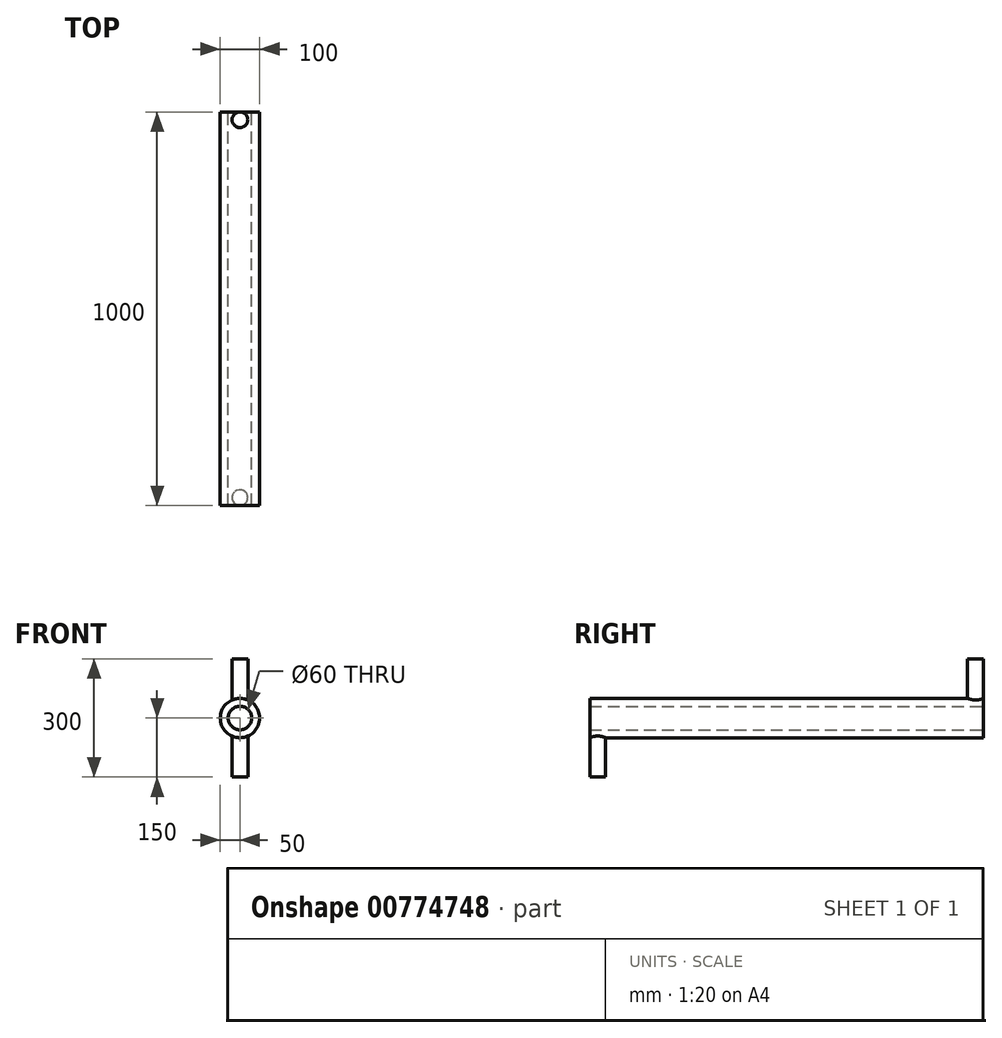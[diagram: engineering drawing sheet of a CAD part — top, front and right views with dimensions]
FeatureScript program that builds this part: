
annotation { "Feature Type Name" : "Feature", "Feature Type Description" : "" }
export const myFeature = defineFeature(function(context is Context, id is Id, definition is map)
    precondition{}
    {
        {
            var Q0;
            Q0=qCreatedBy(makeId("Front.planeOp"),FACE);
            var sketch = newSketch(context, id + "F0", { "sketchPlane" : qUnion([Q0])});
            skCircle(sketch, "E0", {"center": v(0, 0) * mm, "radius": 30 * mm});
            skCircle(sketch, "E1", {"center": v(0, 0) * mm, "radius": 50 * mm});
            skSolve(sketch);
        }
        {
            var Q0;
            Q0=makeQuery(id+"F0.imprint","IMPRINT",FACE,{"disambiguationData":[TD([[makeQuery(id+"F0.imprint","IMPRINT",EDGE,{"derivedFrom":sQuery(id+"F0.wireOp",EDGE,"E0")}),-1.0]])]});
            extrude(context, id + "F1", {"entities" : qUnion([Q0]), "depth" : 1000 * mm, "offsetDistance" : 25 * mm});
        }
        {
            var Q0;
            Q0=qCreatedBy(makeId("Top.planeOp"),FACE);
            cPlane(context, id + "F2", {"entities" : qUnion([Q0]), "cplaneType" : CPlaneType.OFFSET, "offset" : 150 * mm, "width" : 150 * mm, "height" : 150 * mm});
        }
        {
            var Q0;
            Q0=qCreatedBy(makeId("Top.planeOp"),FACE);
            cPlane(context, id + "F3", {"entities" : qUnion([Q0]), "cplaneType" : CPlaneType.OFFSET, "offset" : 150 * mm, "oppositeDirection" : true, "width" : 150 * mm, "height" : 150 * mm});
        }
        {
            var Q0;
            Q0=qCreatedBy(id+"F2.planeOp",FACE);
            var sketch = newSketch(context, id + "F4", { "sketchPlane" : qUnion([Q0])});
            skCircle(sketch, "E2", {"center": v(0, -20) * mm, "radius": 20 * mm});
            skSolve(sketch);
        }
        {
            var Q0;
            Q0=makeQuery(id+"F4.imprint","IMPRINT",FACE,{"disambiguationData":[TD([[makeQuery(id+"F4.imprint","IMPRINT",EDGE,{"derivedFrom":sQuery(id+"F4.wireOp",EDGE,"E2")}),1.0]])]});
            var Q1;
            Q1=makeQuery(id+"F1.opExtrude","SWEPT_FACE",FACE,{"disambiguationData":[OSD([sQuery(id+"F0.wireOp",EDGE,"E1")])]});
            extrude(context, id + "F5", {"entities" : qUnion([Q0]), "operationType" : NewBodyOperationType.ADD, "endBound" : BoundingType.UP_TO_SURFACE, "oppositeDirection" : true, "depth" : 25 * mm, "endBoundEntityFace" : qUnion([Q1]), "offsetDistance" : 25 * mm});
        }
        {
            var Q0;
            Q0=qCreatedBy(id+"F3.planeOp",FACE);
            var sketch = newSketch(context, id + "F6", { "sketchPlane" : qUnion([Q0])});
            skCircle(sketch, "E3", {"center": v(0, -980) * mm, "radius": 20 * mm});
            skSolve(sketch);
        }
        {
            var Q0;
            Q0=makeQuery(id+"F6.imprint","IMPRINT",FACE,{"disambiguationData":[TD([[makeQuery(id+"F6.imprint","IMPRINT",EDGE,{"derivedFrom":sQuery(id+"F6.wireOp",EDGE,"E3")}),1.0]])]});
            var Q1;
            Q1=makeQuery(id+"F1.opExtrude","SWEPT_FACE",FACE,{"disambiguationData":[OSD([sQuery(id+"F0.wireOp",EDGE,"E1")])]});
            extrude(context, id + "F7", {"entities" : qUnion([Q0]), "operationType" : NewBodyOperationType.ADD, "endBound" : BoundingType.UP_TO_SURFACE, "depth" : 25 * mm, "endBoundEntityFace" : qUnion([Q1]), "offsetDistance" : 25 * mm});
        }
    });
